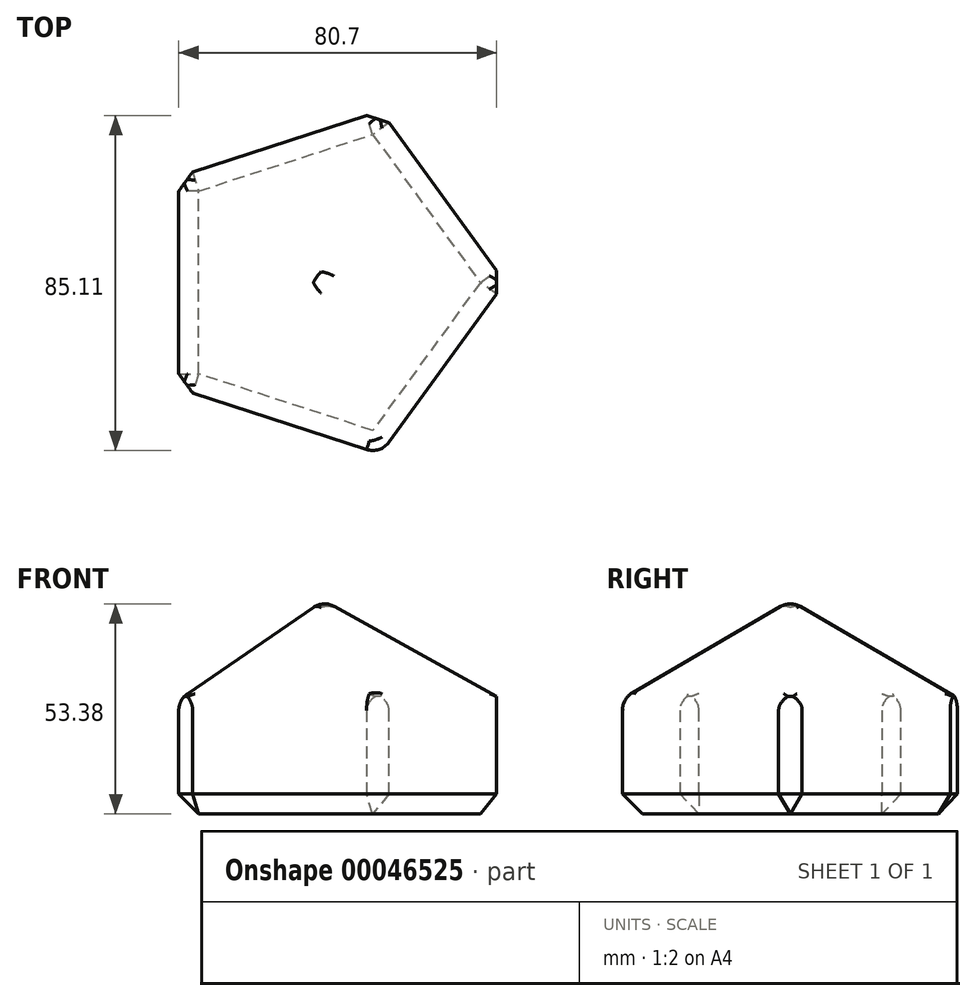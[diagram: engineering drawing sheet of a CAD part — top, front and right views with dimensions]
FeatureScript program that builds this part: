
annotation { "Feature Type Name" : "Feature", "Feature Type Description" : "" }
export const myFeature = defineFeature(function(context is Context, id is Id, definition is map)
    precondition{}
    {
        {
            var Q0;
            Q0=qCreatedBy(makeId("Top.planeOp"),FACE);
            var sketch = newSketch(context, id + "F0", { "sketchPlane" : qUnion([Q0])});
            skCircle(sketch, "E0.cCircle", {"center": v(0, 0) * mm, "radius": 37.06 * mm, "construction": true});
            skLineSegment(sketch, "E0.0", {"start": v(-37.06, -26.93) * mm, "end": v(-37.06, 26.93) * mm});
            skLineSegment(sketch, "E0.1", {"start": v(-37.06, 26.93) * mm, "end": v(14.16, 43.57) * mm});
            skLineSegment(sketch, "E0.2", {"start": v(14.16, 43.57) * mm, "end": v(45.81, 0) * mm});
            skLineSegment(sketch, "E0.3", {"start": v(45.81, 0) * mm, "end": v(14.16, -43.57) * mm});
            skLineSegment(sketch, "E0.4", {"start": v(14.16, -43.57) * mm, "end": v(-37.06, -26.93) * mm});
            skPoint(sketch, "E0.0.midPoint", {"position": v(-37.06, 0) * mm});
            skLineSegment(sketch, "E1", {"start": v(0, 0) * mm, "end": v(14.16, 43.57) * mm});
            skLineSegment(sketch, "E2", {"start": v(45.81, 0) * mm, "end": v(0, 0) * mm});
            skLineSegment(sketch, "E3", {"start": v(14.16, -43.57) * mm, "end": v(0, 0) * mm});
            skLineSegment(sketch, "E4", {"start": v(-37.06, -26.93) * mm, "end": v(0, 0) * mm});
            skLineSegment(sketch, "E5", {"start": v(-37.06, 26.93) * mm, "end": v(0, 0) * mm});
            skSolve(sketch);
        }
        {
            var Q0;
            Q0 = qSketchRegion(id + "F0", true);
            extrude(context, id + "F1", {"entities" : qUnion([Q0]), "depth" : 29.06 * mm});
        }
        {
            var Q0;
            Q0=makeQuery(id+"F1.opExtrude","CAP_FACE",FACE,{"disambiguationData":[OSD([sQuery(id+"F0.wireOp",EDGE,"E0.0"),sQuery(id+"F0.wireOp",EDGE,"E0.1"),sQuery(id+"F0.wireOp",EDGE,"E0.2"),sQuery(id+"F0.wireOp",EDGE,"E0.3"),sQuery(id+"F0.wireOp",EDGE,"E0.4")])],"isStart":false});
            var sketch = newSketch(context, id + "F2", { "sketchPlane" : qUnion([Q0])});
            skLineSegment(sketch, "E6", {"start": v(-37.06, 26.93) * mm, "end": v(0, 0) * mm});
            skLineSegment(sketch, "E7", {"start": v(0, 0) * mm, "end": v(14.16, 43.57) * mm});
            skLineSegment(sketch, "E8", {"start": v(14.16, 43.57) * mm, "end": v(45.81, 0) * mm});
            skLineSegment(sketch, "E9", {"start": v(45.81, 0) * mm, "end": v(0, 0) * mm});
            skLineSegment(sketch, "E10", {"start": v(14.16, -43.57) * mm, "end": v(0, 0) * mm});
            skLineSegment(sketch, "E11", {"start": v(-37.06, -26.93) * mm, "end": v(0, 0) * mm});
            skSolve(sketch);
        }
        {
            var Q0;
            Q0=makeQuery(id+"F2.imprint","IMPRINT",FACE,{"disambiguationData":[TD([[makeQuery(id+"F2.imprint","IMPRINT",EDGE,{"derivedFrom":sQuery(id+"F2.wireOp",EDGE,"E7")}),-1.0]])]});
            cPlane(context, id + "F3", {"entities" : qUnion([Q0]), "cplaneType" : CPlaneType.OFFSET, "offset" : 25.4 * mm, "width" : 152.4 * mm, "height" : 152.4 * mm});
        }
        {
            var Q0;
            Q0=qCreatedBy(id+"F3.planeOp",FACE);
            var sketch = newSketch(context, id + "F4", { "sketchPlane" : qUnion([Q0])});
            skPoint(sketch, "E12", {"position": v(0, 0) * mm});
            skSolve(sketch);
        }
        {
            var Q1;
            Q1=makeQuery(id+"F2.imprint","IMPRINT",FACE,{"disambiguationData":[TD([[makeQuery(id+"F2.imprint","IMPRINT",EDGE,{"derivedFrom":sQuery(id+"F2.wireOp",EDGE,"E6")}),-1.0]])]});
            var Q2;
            Q2=sQuery(id+"F4.wireOp",VERTEX,"E12");
            loft(context, id + "F5", {"operationType" : NewBodyOperationType.ADD, "sheetProfilesArray" : [{ "sheetProfileEntities" : qUnion([Q1]) }, { "sheetProfileEntities" : qUnion([Q2]) }]});
        }
        {
            var Q1;
            Q1=makeQuery(id+"F2.imprint","IMPRINT",FACE,{"disambiguationData":[TD([[makeQuery(id+"F2.imprint","IMPRINT",EDGE,{"derivedFrom":sQuery(id+"F2.wireOp",EDGE,"E6")}),1.0]])]});
            var Q2;
            Q2=sQuery(id+"F4.wireOp",VERTEX,"E12");
            loft(context, id + "F6", {"operationType" : NewBodyOperationType.ADD, "sheetProfilesArray" : [{ "sheetProfileEntities" : qUnion([Q1]) }, { "sheetProfileEntities" : qUnion([Q2]) }]});
        }
        {
            var Q1;
            Q1=makeQuery(id+"F2.imprint","IMPRINT",FACE,{"disambiguationData":[TD([[makeQuery(id+"F2.imprint","IMPRINT",EDGE,{"derivedFrom":sQuery(id+"F2.wireOp",EDGE,"E7")}),-1.0]])]});
            var Q2;
            Q2=sQuery(id+"F4.wireOp",VERTEX,"E12");
            loft(context, id + "F7", {"operationType" : NewBodyOperationType.ADD, "sheetProfilesArray" : [{ "sheetProfileEntities" : qUnion([Q1]) }, { "sheetProfileEntities" : qUnion([Q2]) }]});
        }
        {
            var Q1;
            Q1=makeQuery(id+"F2.imprint","IMPRINT",FACE,{"disambiguationData":[TD([[makeQuery(id+"F2.imprint","IMPRINT",EDGE,{"derivedFrom":sQuery(id+"F2.wireOp",EDGE,"E9")}),1.0]])]});
            var Q2;
            Q2=sQuery(id+"F4.wireOp",VERTEX,"E12");
            loft(context, id + "F8", {"operationType" : NewBodyOperationType.ADD, "sheetProfilesArray" : [{ "sheetProfileEntities" : qUnion([Q1]) }, { "sheetProfileEntities" : qUnion([Q2]) }]});
        }
        {
            var Q1;
            Q1=makeQuery(id+"F2.imprint","IMPRINT",FACE,{"disambiguationData":[TD([[makeQuery(id+"F2.imprint","IMPRINT",EDGE,{"derivedFrom":sQuery(id+"F2.wireOp",EDGE,"E10")}),1.0]])]});
            var Q2;
            Q2=sQuery(id+"F4.wireOp",VERTEX,"E12");
            loft(context, id + "F9", {"operationType" : NewBodyOperationType.ADD, "sheetProfilesArray" : [{ "sheetProfileEntities" : qUnion([Q1]) }, { "sheetProfileEntities" : qUnion([Q2]) }]});
        }
        {
            var Q0;
            Q0=makeQuery(id+"F5.opLoft","SWEPT_FACE",FACE,{"disambiguationData":[OSD([sQuery(id+"F0.wireOp",EDGE,"E0.0"),sQuery(id+"F0.wireOp",EDGE,"E0.1"),sQuery(id+"F0.wireOp",EDGE,"E0.4"),sQuery(id+"F2.wireOp",EDGE,"E6"),sQuery(id+"F2.wireOp",EDGE,"E11")])]});
            fillet(context, id + "F10", {"entities" : qUnion([Q0]), "radius" : 5.08 * mm, "tangentPropagation" : true, "allowEdgeOverflow" : false});
        }
        {
            var Q0;
            Q0=makeQuery(id+"F6.opLoft","SWEPT_FACE",FACE,{"disambiguationData":[OSD([sQuery(id+"F0.wireOp",EDGE,"E0.0"),sQuery(id+"F0.wireOp",EDGE,"E0.1"),sQuery(id+"F2.wireOp",EDGE,"E6"),sQuery(id+"F2.wireOp",EDGE,"E7"),sQuery(id+"F2.wireOp",EDGE,"E8")])]});
            fillet(context, id + "F11", {"entities" : qUnion([Q0]), "radius" : 5.08 * mm, "tangentPropagation" : true, "allowEdgeOverflow" : false});
        }
        {
            var Q0;
            Q0=makeQuery(id+"F7.opLoft","SWEPT_FACE",FACE,{"disambiguationData":[OSD([sQuery(id+"F0.wireOp",EDGE,"E0.1"),sQuery(id+"F0.wireOp",EDGE,"E0.3"),sQuery(id+"F2.wireOp",EDGE,"E7"),sQuery(id+"F2.wireOp",EDGE,"E8"),sQuery(id+"F2.wireOp",EDGE,"E9")])]});
            fillet(context, id + "F12", {"entities" : qUnion([Q0]), "radius" : 5.08 * mm, "tangentPropagation" : true, "allowEdgeOverflow" : false});
        }
        {
            var Q0;
            Q0=makeQuery(id+"F8.opLoft","SWEPT_FACE",FACE,{"disambiguationData":[OSD([sQuery(id+"F0.wireOp",EDGE,"E0.3"),sQuery(id+"F0.wireOp",EDGE,"E0.4"),sQuery(id+"F2.wireOp",EDGE,"E8"),sQuery(id+"F2.wireOp",EDGE,"E9"),sQuery(id+"F2.wireOp",EDGE,"E10")])]});
            fillet(context, id + "F13", {"entities" : qUnion([Q0]), "radius" : 5.08 * mm, "tangentPropagation" : true, "allowEdgeOverflow" : false});
        }
        {
            var Q0;
            Q0=makeQuery(id+"F9.opLoft","SWEPT_FACE",FACE,{"disambiguationData":[OSD([sQuery(id+"F0.wireOp",EDGE,"E0.0"),sQuery(id+"F0.wireOp",EDGE,"E0.3"),sQuery(id+"F0.wireOp",EDGE,"E0.4"),sQuery(id+"F2.wireOp",EDGE,"E10"),sQuery(id+"F2.wireOp",EDGE,"E11")])]});
            fillet(context, id + "F14", {"entities" : qUnion([Q0]), "radius" : 5.08 * mm, "tangentPropagation" : true, "allowEdgeOverflow" : false});
        }
        {
            var Q0;
            Q0=makeQuery(id+"F1.opExtrude","SWEPT_FACE",FACE,{"disambiguationData":[OSD([sQuery(id+"F0.wireOp",EDGE,"E0.4")])]});
            var Q1;
            Q1=makeQuery(id+"F1.opExtrude","SWEPT_FACE",FACE,{"disambiguationData":[OSD([sQuery(id+"F0.wireOp",EDGE,"E0.3")])]});
            var Q2;
            Q2=makeQuery(id+"F1.opExtrude","SWEPT_FACE",FACE,{"disambiguationData":[OSD([sQuery(id+"F0.wireOp",EDGE,"E0.2")])]});
            var Q3;
            Q3=makeQuery(id+"F1.opExtrude","SWEPT_FACE",FACE,{"disambiguationData":[OSD([sQuery(id+"F0.wireOp",EDGE,"E0.1")])]});
            var Q4;
            Q4=makeQuery(id+"F1.opExtrude","SWEPT_FACE",FACE,{"disambiguationData":[OSD([sQuery(id+"F0.wireOp",EDGE,"E0.0")])]});
            chamfer(context, id + "F15", {"entities" : qUnion([Q0, Q1, Q2, Q3, Q4]), "width" : 5.08 * mm, "tangentPropagation" : true});
        }
    });
